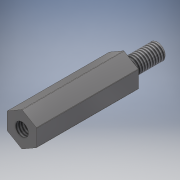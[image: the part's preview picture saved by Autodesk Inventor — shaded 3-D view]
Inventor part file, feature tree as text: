
AUTODESK INVENTOR PART (.ipt)
format: ipt  version: 2016 (Build 200138000, 138)  size: 146,944 bytes
history: native  units: in
note: dims shown in document units (in); Inventor stores cm internally (conversion verified against a paired STEP export)
features: sketch x3, extrude x2, fillet x2, hole x1, thread x1
ambient origin geometry x8: Origin, YZ Plane, XZ Plane, XY Plane, X Axis, Y Axis, Z Axis, Center Point
bodies: Solid1 (feature_tree)
feature tree (9):
  extrude  "Extrusion1"  Depth=0.748in
  hole  "Hole1"  [1 undecoded]
  fillet  "Fillet1"  Radius=0.1181in
  extrude  "Extrusion2"  Depth=0.0079in TaperAngle=0.0deg
  thread  "Thread1"  [1 undecoded]
  fillet  "Fillet2"  [1 undecoded]
  sketch  "Sketch1"  dims[d18=0.748in d19=0.0in d20=0.1181in]
  sketch  "Sketch2"  dims[d21=0.0968in d22=0.2362in d23=0.1575in d24=0.0787in d25=90.0deg d26=0.3465in d27=0.8108in d28=0.0039in d29=0.1181in]
  sketch  "Sketch4"  dims[d30=0.252in d31=0.0in d32=0.3924in d33=0.0in d34=0.0079in]
note: 3 required parameter values undecoded (feature->parameter linkage not recoverable at this tier; creation-order binding heuristic only, values carry confidence <= 0.55)
